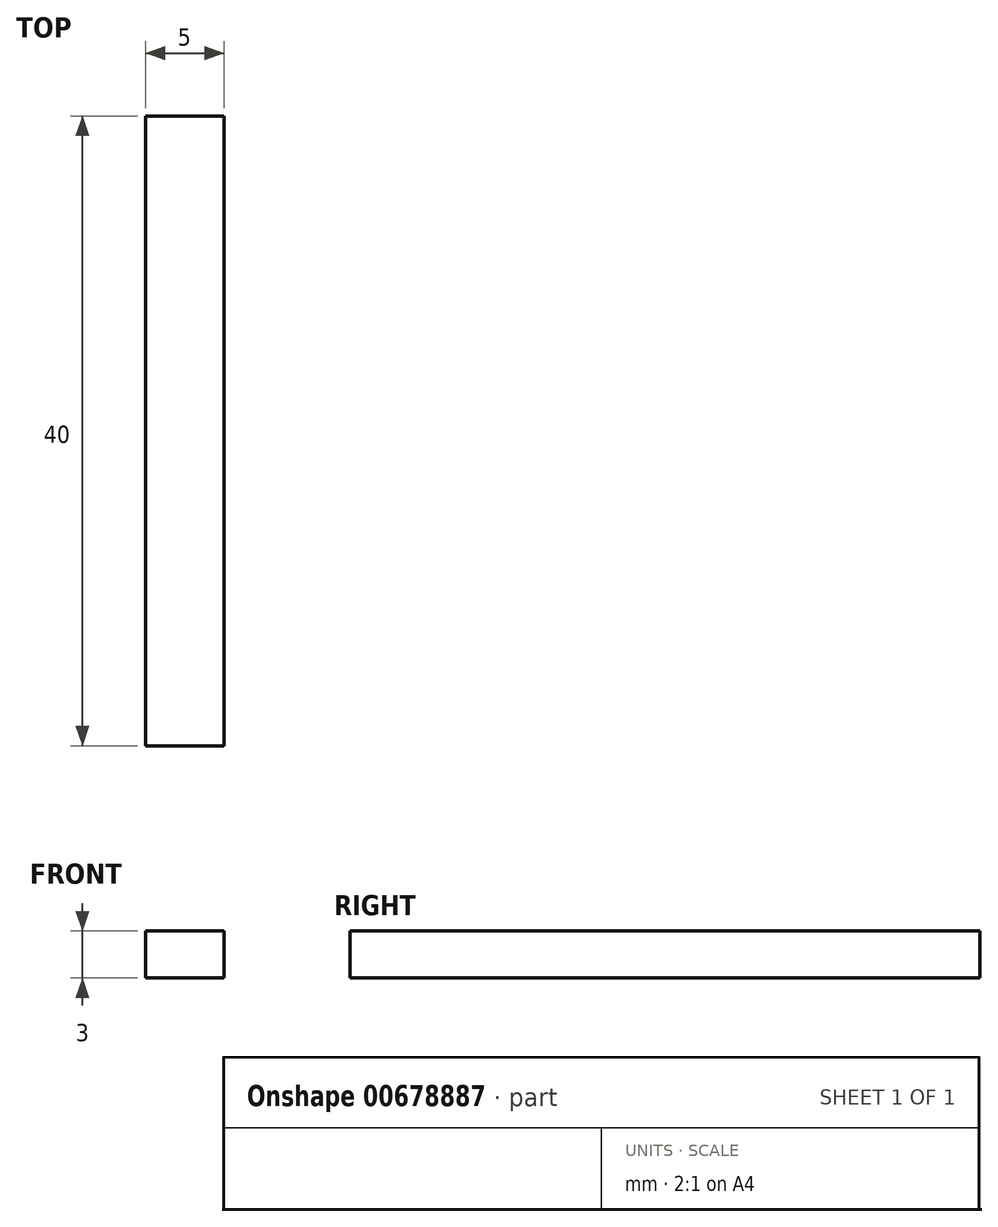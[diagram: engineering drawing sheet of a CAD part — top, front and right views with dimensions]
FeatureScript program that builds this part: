
annotation { "Feature Type Name" : "Feature", "Feature Type Description" : "" }
export const myFeature = defineFeature(function(context is Context, id is Id, definition is map)
    precondition{}
    {
        {
            var Q0;
            Q0=qCreatedBy(makeId("Top.planeOp"),FACE);
            var sketch = newSketch(context, id + "F0", { "sketchPlane" : qUnion([Q0])});
            skLineSegment(sketch, "E0.bottom", {"start": v(-40.63, -0.9) * mm, "end": v(-35.63, -0.9) * mm});
            skLineSegment(sketch, "E0.top", {"start": v(-40.63, 39.1) * mm, "end": v(-35.63, 39.1) * mm});
            skLineSegment(sketch, "E0.left", {"start": v(-40.63, -0.9) * mm, "end": v(-40.63, 39.1) * mm});
            skLineSegment(sketch, "E0.right", {"start": v(-35.63, -0.9) * mm, "end": v(-35.63, 39.1) * mm});
            skSolve(sketch);
        }
        {
            var Q0;
            Q0=makeQuery(id+"F0.imprint","IMPRINT",FACE,{"disambiguationData":[TD([[makeQuery(id+"F0.imprint","IMPRINT",EDGE,{"derivedFrom":sQuery(id+"F0.wireOp",EDGE,"E0.bottom")}),1.0]])]});
            extrude(context, id + "F1", {"entities" : qUnion([Q0]), "depth" : 3 * mm, "offsetDistance" : 25.4 * mm});
        }
    });
